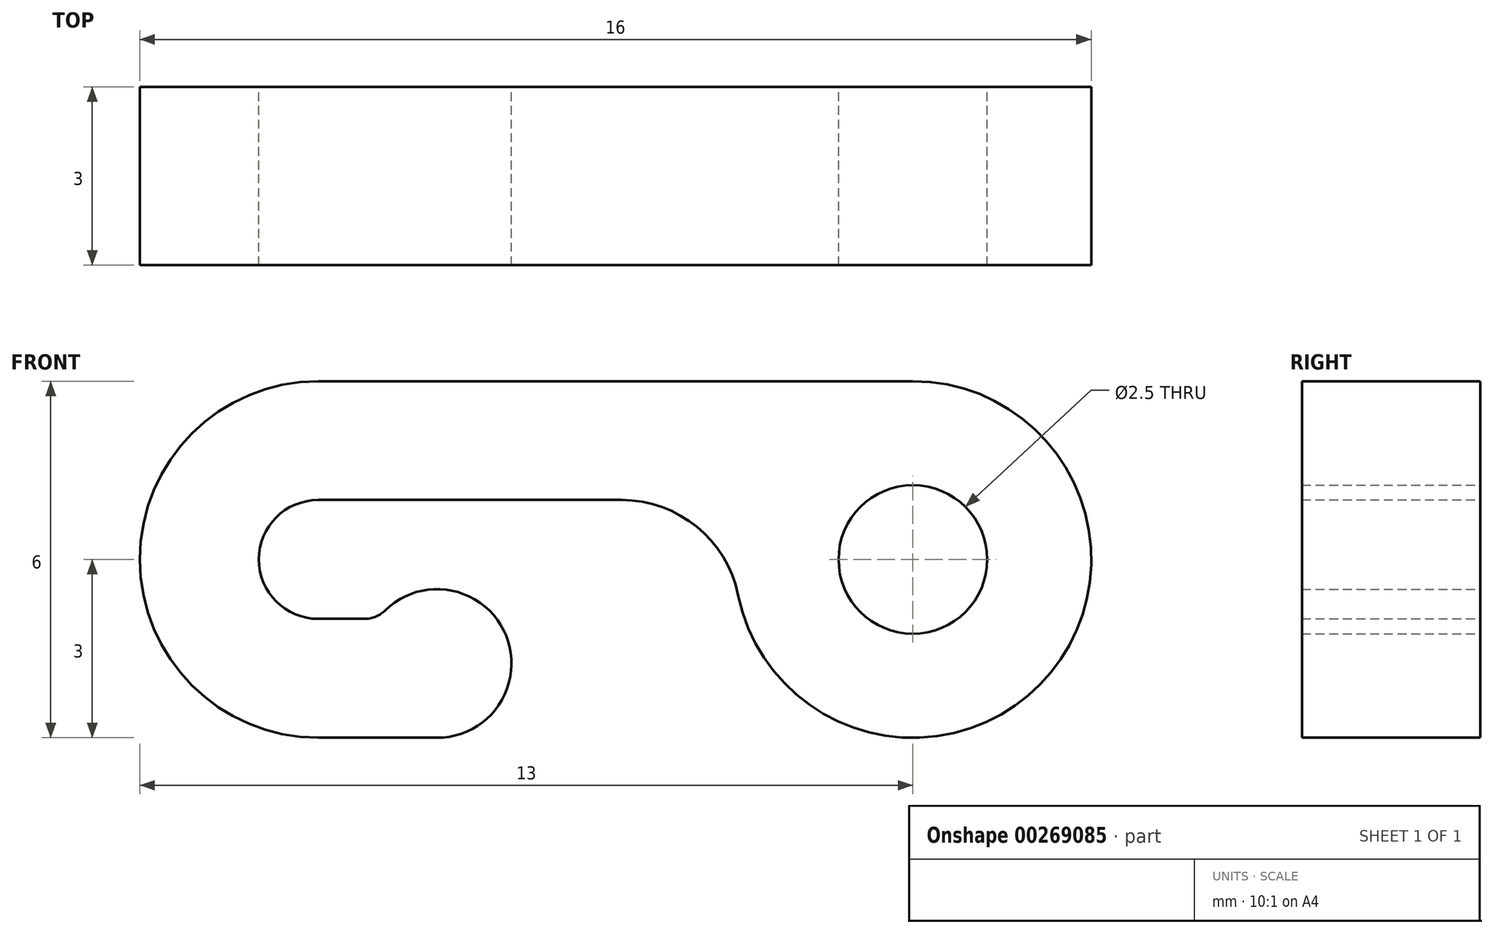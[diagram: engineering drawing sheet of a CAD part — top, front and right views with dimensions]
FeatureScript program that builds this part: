
annotation { "Feature Type Name" : "Feature", "Feature Type Description" : "" }
export const myFeature = defineFeature(function(context is Context, id is Id, definition is map)
    precondition{}
    {
        {
            var Q0;
            Q0=qCreatedBy(makeId("Front.planeOp"),FACE);
            var sketch = newSketch(context, id + "F0", { "sketchPlane" : qUnion([Q0])});
            skCircle(sketch, "E0", {"center": v(0, 0) * mm, "radius": 1.25 * mm});
            skArc(sketch, "E1", {"start": v(-10, 1) * mm, "mid": v(-11, 0) * mm, "end": v(-10, -1) * mm});
            skArc(sketch, "E2", {"start": v(-10, 3) * mm, "mid": v(-13, 0) * mm, "end": v(-10, -3) * mm});
            skArc(sketch, "E3", {"start": v(-2.94, -0.6) * mm, "mid": v(2.32, -1.9) * mm, "end": v(0, 3) * mm});
            skLineSegment(sketch, "E4", {"start": v(0, 3) * mm, "end": v(-10, 3) * mm});
            skLineSegment(sketch, "E5", {"start": v(-8, -3) * mm, "end": v(-10, -3) * mm});
            skLineSegment(sketch, "E6", {"start": v(-10, 1) * mm, "end": v(-4.9, 1) * mm});
            skLineSegment(sketch, "E7", {"start": v(-10, -0.5) * mm, "end": v(-10, -3) * mm});
            skLineSegment(sketch, "E8", {"start": v(-10, -1) * mm, "end": v(-9.22, -1) * mm});
            skLineSegment(sketch, "E9", {"start": v(-10, 0) * mm, "end": v(-10, -1) * mm});
            skArc(sketch, "E10", {"start": v(-8, -3) * mm, "mid": v(-6.84, -1.28) * mm, "end": v(-8.87, -0.86) * mm});
            skPoint(sketch, "E11.orphan", {"position": v(0, -3) * mm});
            skPoint(sketch, "E12.start.orphan", {"position": v(-8, -0.5) * mm});
            skPoint(sketch, "E13.visualSharp", {"position": v(-2.83, 1) * mm});
            skArc(sketch, "E13.filletArc", {"start": v(-2.94, -0.6) * mm, "mid": v(-3.63, 0.55) * mm, "end": v(-4.9, 1) * mm});
            skPoint(sketch, "E14.visualSharp", {"position": v(-9, -1) * mm});
            skArc(sketch, "E14.filletArc", {"start": v(-9.22, -1) * mm, "mid": v(-9.04, -0.96) * mm, "end": v(-8.87, -0.86) * mm});
            skSolve(sketch);
        }
        {
            var Q0;
            Q0 = qSketchRegion(id + "F0", true);
            extrude(context, id + "F1", {"entities" : qUnion([Q0]), "depth" : 3 * mm});
        }
    });
